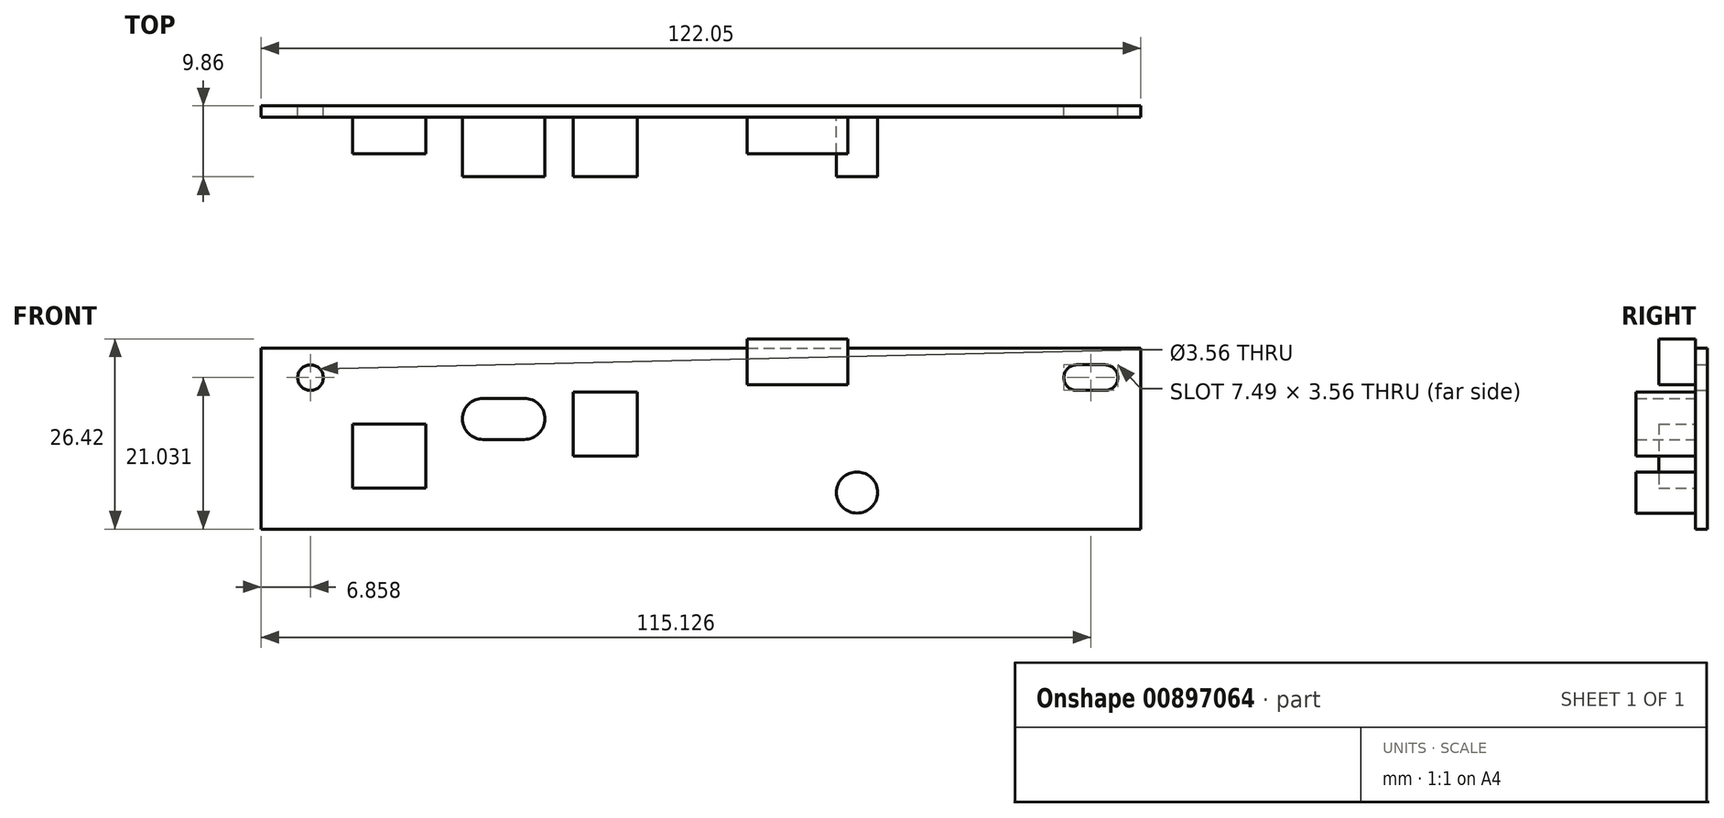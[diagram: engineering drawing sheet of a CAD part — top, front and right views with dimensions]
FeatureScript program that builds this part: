
annotation { "Feature Type Name" : "Feature", "Feature Type Description" : "" }
export const myFeature = defineFeature(function(context is Context, id is Id, definition is map)
    precondition{}
    {
        {
            var Q0;
            Q0=qCreatedBy(makeId("Front.planeOp"),FACE);
            var sketch = newSketch(context, id + "F0", { "sketchPlane" : qUnion([Q0])});
            skLineSegment(sketch, "E0.bottom", {"start": v(0, 0) * mm, "end": v(122.05, 0) * mm});
            skLineSegment(sketch, "E0.top", {"start": v(0, 25.15) * mm, "end": v(122.05, 25.15) * mm});
            skLineSegment(sketch, "E0.left", {"start": v(0, 0) * mm, "end": v(0, 25.15) * mm});
            skLineSegment(sketch, "E0.right", {"start": v(122.05, 0) * mm, "end": v(122.05, 25.15) * mm});
            skCircle(sketch, "E1", {"center": v(6.86, 21.03) * mm, "radius": 1.78 * mm});
            skLineSegment(sketch, "E2", {"start": v(113.16, 22.8) * mm, "end": v(117.1, 22.8) * mm});
            skLineSegment(sketch, "E3", {"start": v(113.16, 19.25) * mm, "end": v(117.1, 19.25) * mm});
            skLineSegment(sketch, "E4", {"start": v(113.16, 22.8) * mm, "end": v(113.16, 19.25) * mm});
            skLineSegment(sketch, "E5", {"start": v(117.1, 22.8) * mm, "end": v(117.1, 19.25) * mm});
            skArc(sketch, "E6", {"start": v(113.16, 22.8) * mm, "mid": v(111.38, 21.03) * mm, "end": v(113.16, 19.25) * mm});
            skArc(sketch, "E7", {"start": v(117.1, 22.8) * mm, "mid": v(118.87, 21.03) * mm, "end": v(117.1, 19.25) * mm});
            skSolve(sketch);
        }
        {
            var Q0;
            Q0 = qSketchRegion(id + "F0", true);
            extrude(context, id + "F1", {"entities" : qUnion([Q0]), "depth" : 1.6 * mm, "offsetDistance" : 25.4 * mm});
        }
        {
            var Q0;
            Q0=makeQuery(id+"F1.opExtrude","CAP_FACE",FACE,{"disambiguationData":[OSD([sQuery(id+"F0.wireOp",EDGE,"E0.bottom"),sQuery(id+"F0.wireOp",EDGE,"E0.top"),sQuery(id+"F0.wireOp",EDGE,"E0.left"),sQuery(id+"F0.wireOp",EDGE,"E0.right"),sQuery(id+"F0.wireOp",EDGE,"E1"),sQuery(id+"F0.wireOp",EDGE,"E2"),sQuery(id+"F0.wireOp",EDGE,"E3"),sQuery(id+"F0.wireOp",EDGE,"E6"),sQuery(id+"F0.wireOp",EDGE,"E7")])],"isStart":false});
            var sketch = newSketch(context, id + "F2", { "sketchPlane" : qUnion([Q0])});
            skLineSegment(sketch, "E8.bottom", {"start": v(12.7, 14.6) * mm, "end": v(22.86, 14.6) * mm});
            skLineSegment(sketch, "E8.top", {"start": v(12.7, 5.72) * mm, "end": v(22.86, 5.72) * mm});
            skLineSegment(sketch, "E8.left", {"start": v(12.7, 14.6) * mm, "end": v(12.7, 5.71) * mm});
            skLineSegment(sketch, "E8.right", {"start": v(22.86, 14.6) * mm, "end": v(22.86, 5.71) * mm});
            skLineSegment(sketch, "E9.bottom", {"start": v(67.44, 26.42) * mm, "end": v(81.4, 26.42) * mm});
            skLineSegment(sketch, "E9.top", {"start": v(67.44, 20.07) * mm, "end": v(81.4, 20.07) * mm});
            skLineSegment(sketch, "E9.left", {"start": v(67.44, 26.42) * mm, "end": v(67.44, 20.07) * mm});
            skLineSegment(sketch, "E9.right", {"start": v(81.4, 26.42) * mm, "end": v(81.4, 20.07) * mm});
            skSolve(sketch);
        }
        {
            var Q0;
            Q0 = qSketchRegion(id + "F2", true);
            extrude(context, id + "F3", {"entities" : qUnion([Q0]), "operationType" : NewBodyOperationType.ADD, "depth" : 5.08 * mm, "offsetDistance" : 25.4 * mm});
        }
        {
            var Q0;
            Q0=makeQuery(id+"F1.opExtrude","CAP_FACE",FACE,{"disambiguationData":[OSD([sQuery(id+"F0.wireOp",EDGE,"E0.bottom"),sQuery(id+"F0.wireOp",EDGE,"E0.top"),sQuery(id+"F0.wireOp",EDGE,"E0.left"),sQuery(id+"F0.wireOp",EDGE,"E0.right"),sQuery(id+"F0.wireOp",EDGE,"E1"),sQuery(id+"F0.wireOp",EDGE,"E2"),sQuery(id+"F0.wireOp",EDGE,"E3"),sQuery(id+"F0.wireOp",EDGE,"E6"),sQuery(id+"F0.wireOp",EDGE,"E7")])],"isStart":false});
            var sketch = newSketch(context, id + "F4", { "sketchPlane" : qUnion([Q0])});
            skLineSegment(sketch, "E10.bottom", {"start": v(43.3, 19.05) * mm, "end": v(52.2, 19.05) * mm});
            skLineSegment(sketch, "E10.top", {"start": v(43.3, 10.16) * mm, "end": v(52.2, 10.16) * mm});
            skLineSegment(sketch, "E10.left", {"start": v(43.3, 19.05) * mm, "end": v(43.3, 10.16) * mm});
            skLineSegment(sketch, "E10.right", {"start": v(52.2, 19.05) * mm, "end": v(52.2, 10.16) * mm});
            skCircle(sketch, "E11", {"center": v(82.68, 5.08) * mm, "radius": 2.86 * mm});
            skLineSegment(sketch, "E12.bottom", {"start": v(30.8, 18.16) * mm, "end": v(36.51, 18.16) * mm});
            skLineSegment(sketch, "E12.top", {"start": v(30.8, 12.45) * mm, "end": v(36.51, 12.45) * mm});
            skLineSegment(sketch, "E12.left", {"start": v(30.8, 18.16) * mm, "end": v(30.8, 12.45) * mm});
            skLineSegment(sketch, "E12.right", {"start": v(36.51, 18.16) * mm, "end": v(36.51, 12.45) * mm});
            skArc(sketch, "E13", {"start": v(30.8, 18.16) * mm, "mid": v(27.94, 15.3) * mm, "end": v(30.8, 12.45) * mm});
            skArc(sketch, "E14", {"start": v(36.51, 18.16) * mm, "mid": v(39.37, 15.3) * mm, "end": v(36.51, 12.45) * mm});
            skSolve(sketch);
        }
        {
            var Q0;
            Q0 = qSketchRegion(id + "F4", true);
            extrude(context, id + "F5", {"entities" : qUnion([Q0]), "operationType" : NewBodyOperationType.ADD, "depth" : 8.25 * mm, "offsetDistance" : 25.4 * mm});
        }
    });
